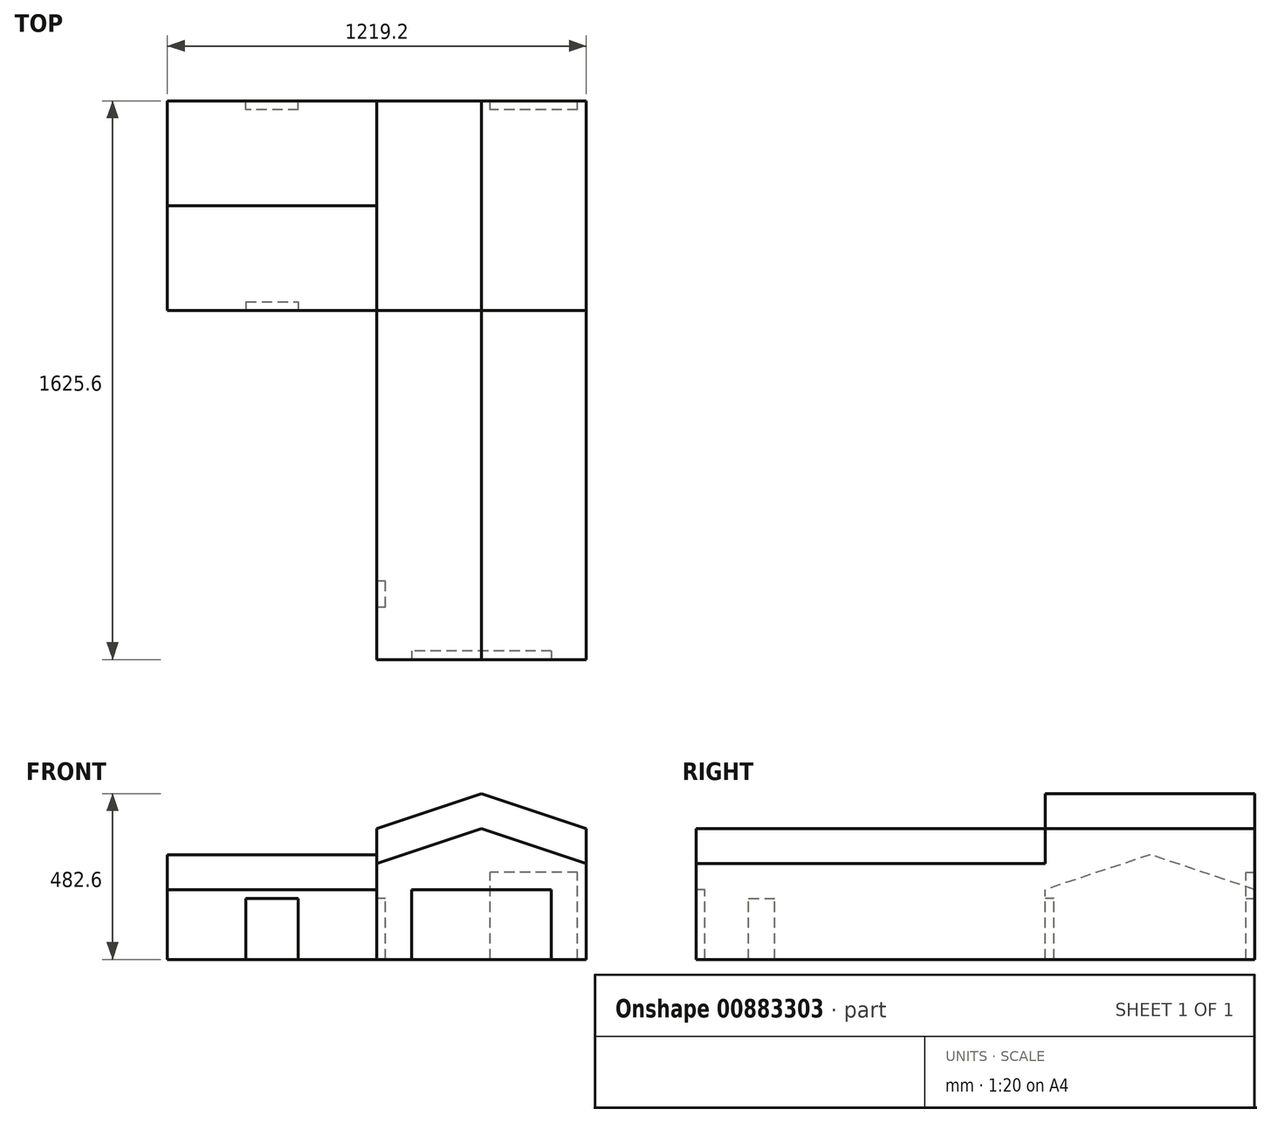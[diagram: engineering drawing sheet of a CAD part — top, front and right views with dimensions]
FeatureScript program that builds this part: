
annotation { "Feature Type Name" : "Feature", "Feature Type Description" : "" }
export const myFeature = defineFeature(function(context is Context, id is Id, definition is map)
    precondition{}
    {
        {
            var Q0;
            Q0=qCreatedBy(makeId("Front.planeOp"),FACE);
            var sketch = newSketch(context, id + "F0", { "sketchPlane" : qUnion([Q0])});
            skLineSegment(sketch, "E0", {"start": v(0, 0) * mm, "end": v(-304.8, 0) * mm});
            skLineSegment(sketch, "E1", {"start": v(-304.8, 0) * mm, "end": v(-304.8, 279.4) * mm});
            skLineSegment(sketch, "E2", {"start": v(-304.8, 279.4) * mm, "end": v(0, 381) * mm});
            skLineSegment(sketch, "E3", {"start": v(0, 381) * mm, "end": v(0, 0) * mm, "construction": true});
            skLineSegment(sketch, "E4.MirrorCS", {"start": v(304.8, 279.4) * mm, "end": v(0, 381) * mm});
            skLineSegment(sketch, "E5.MirrorCS", {"start": v(304.8, 0) * mm, "end": v(304.8, 279.4) * mm});
            skLineSegment(sketch, "E6.MirrorCS", {"start": v(0, 0) * mm, "end": v(304.8, 0) * mm});
            skSolve(sketch);
        }
        {
            var Q0;
            Q0=makeQuery(id+"F0.imprint","IMPRINT",FACE,{"disambiguationData":[TD([[makeQuery(id+"F0.imprint","IMPRINT",EDGE,{"derivedFrom":sQuery(id+"F0.wireOp",EDGE,"E0")}),-1.0]])]});
            extrude(context, id + "F1", {"entities" : qUnion([Q0]), "depth" : 1016 * mm, "offsetDistance" : 25.4 * mm});
        }
        {
            var Q0;
            Q0=makeQuery(id+"F1.opExtrude","CAP_FACE",FACE,{"disambiguationData":[OSD([sQuery(id+"F0.wireOp",EDGE,"E0"),sQuery(id+"F0.wireOp",EDGE,"E1"),sQuery(id+"F0.wireOp",EDGE,"E2"),sQuery(id+"F0.wireOp",EDGE,"E4.MirrorCS"),sQuery(id+"F0.wireOp",EDGE,"E5.MirrorCS"),sQuery(id+"F0.wireOp",EDGE,"E6.MirrorCS")])],"isStart":true});
            var sketch = newSketch(context, id + "F2", { "sketchPlane" : qUnion([Q0])});
            skLineSegment(sketch, "E7.0", {"start": v(-304.8, 0) * mm, "end": v(304.8, 0) * mm});
            skLineSegment(sketch, "E8", {"start": v(304.8, 381) * mm, "end": v(304.8, 0) * mm});
            skLineSegment(sketch, "E9", {"start": v(-304.8, 0) * mm, "end": v(-304.8, 381) * mm});
            skLineSegment(sketch, "E10", {"start": v(0, 0) * mm, "end": v(0, 482.6) * mm, "construction": true});
            skLineSegment(sketch, "E11", {"start": v(-304.8, 381) * mm, "end": v(0, 482.6) * mm});
            skLineSegment(sketch, "E12", {"start": v(0, 482.6) * mm, "end": v(304.8, 381) * mm});
            skSolve(sketch);
        }
        {
            var Q0;
            Q0 = qSketchRegion(id + "F2", true);
            extrude(context, id + "F3", {"entities" : qUnion([Q0]), "operationType" : NewBodyOperationType.ADD, "depth" : 609.6 * mm, "offsetDistance" : 25.4 * mm});
        }
        {
            var Q0;
            Q0=makeQuery(id+"F3.boolean.opBoolean","MERGE",FACE,{"derivedFrom":[makeQuery(id+"F1.opExtrude","SWEPT_FACE",FACE,{"disambiguationData":[OSD([sQuery(id+"F0.wireOp",EDGE,"E1")])]}),makeQuery(id+"F3.opExtrude","SWEPT_FACE",FACE,{"disambiguationData":[OSD([sQuery(id+"F2.wireOp",EDGE,"E8")])]})]});
            var sketch = newSketch(context, id + "F4", { "sketchPlane" : qUnion([Q0])});
            skLineSegment(sketch, "E13", {"start": v(-609.6, 0) * mm, "end": v(-609.6, 203.2) * mm});
            skLineSegment(sketch, "E14.0", {"start": v(-609.6, 381) * mm, "end": v(0, 381) * mm});
            skLineSegment(sketch, "E15", {"start": v(-304.8, 381) * mm, "end": v(-304.8, 0) * mm, "construction": true});
            skLineSegment(sketch, "E16.MirrorCS", {"start": v(0, 0) * mm, "end": v(0, 203.2) * mm});
            skLineSegment(sketch, "E17", {"start": v(-304.8, 0) * mm, "end": v(-304.8, 304.8) * mm});
            skLineSegment(sketch, "E18", {"start": v(-609.6, 203.2) * mm, "end": v(-304.8, 304.8) * mm});
            skLineSegment(sketch, "E19", {"start": v(-304.8, 304.8) * mm, "end": v(0, 203.2) * mm});
            skSolve(sketch);
        }
        {
            var Q0;
            {var subQ0=sQuery(id+"F4.wireOp",EDGE,"E13");Q0=makeQuery(id+"F4.imprint","IMPRINT",FACE,{"disambiguationData":[TD([[makeQuery(id+"F4.imprint","IMPRINT",EDGE,{"derivedFrom":subQ0}),-1.0]])]});}
            var Q1;
            {var subQ0=sQuery(id+"F4.wireOp",EDGE,"E16.MirrorCS");Q1=makeQuery(id+"F4.imprint","IMPRINT",FACE,{"disambiguationData":[TD([[makeQuery(id+"F4.imprint","IMPRINT",EDGE,{"derivedFrom":subQ0}),1.0]])]});}
            extrude(context, id + "F5", {"entities" : qUnion([Q0, Q1]), "operationType" : NewBodyOperationType.ADD, "depth" : 609.6 * mm, "offsetDistance" : 25.4 * mm});
        }
        {
            var Q0;
            Q0=makeQuery(id+"F5.opExtrude","SWEPT_FACE",FACE,{"disambiguationData":[OSD([sQuery(id+"F4.wireOp",EDGE,"E16.MirrorCS")])]});
            var sketch = newSketch(context, id + "F6", { "sketchPlane" : qUnion([Q0])});
            skLineSegment(sketch, "E20", {"start": v(-609.6, 0) * mm, "end": v(-609.6, 177.8) * mm, "construction": true});
            skLineSegment(sketch, "E21.0", {"start": v(-685.8, 0) * mm, "end": v(-685.8, 177.8) * mm});
            skLineSegment(sketch, "E22.0", {"start": v(-533.4, 0) * mm, "end": v(-533.4, 177.8) * mm});
            skLineSegment(sketch, "E23.0", {"start": v(-685.8, 177.8) * mm, "end": v(-533.4, 177.8) * mm});
            skPoint(sketch, "E24.orphan", {"position": v(-609.6, 203.2) * mm});
            skSolve(sketch);
        }
        {
            var Q0;
            {var subQ0=sQuery(id+"F6.wireOp",EDGE,"E21.0");Q0=makeQuery(id+"F6.imprint","IMPRINT",FACE,{"disambiguationData":[TD([[makeQuery(id+"F6.imprint","IMPRINT",EDGE,{"derivedFrom":subQ0}),-1.0]])]});}
            extrude(context, id + "F7", {"entities" : qUnion([Q0]), "operationType" : NewBodyOperationType.REMOVE, "oppositeDirection" : true, "depth" : 25.4 * mm, "offsetDistance" : 25.4 * mm});
        }
        {
            var Q0;
            Q0=makeQuery(id+"F1.opExtrude","CAP_FACE",FACE,{"disambiguationData":[OSD([sQuery(id+"F0.wireOp",EDGE,"E0"),sQuery(id+"F0.wireOp",EDGE,"E1"),sQuery(id+"F0.wireOp",EDGE,"E2"),sQuery(id+"F0.wireOp",EDGE,"E4.MirrorCS"),sQuery(id+"F0.wireOp",EDGE,"E5.MirrorCS"),sQuery(id+"F0.wireOp",EDGE,"E6.MirrorCS")])],"isStart":false});
            var sketch = newSketch(context, id + "F8", { "sketchPlane" : qUnion([Q0])});
            skLineSegment(sketch, "E25", {"start": v(0, 0) * mm, "end": v(0, 203.2) * mm, "construction": true});
            skLineSegment(sketch, "E26.0", {"start": v(-203.2, 0) * mm, "end": v(-203.2, 203.2) * mm});
            skLineSegment(sketch, "E27.0", {"start": v(203.2, 0) * mm, "end": v(203.2, 203.2) * mm});
            skLineSegment(sketch, "E28.0", {"start": v(203.2, 203.2) * mm, "end": v(-203.2, 203.2) * mm});
            skSolve(sketch);
        }
        {
            var Q0;
            {var subQ0=sQuery(id+"F8.wireOp",EDGE,"E26.0");Q0=makeQuery(id+"F8.imprint","IMPRINT",FACE,{"disambiguationData":[TD([[makeQuery(id+"F8.imprint","IMPRINT",EDGE,{"derivedFrom":subQ0}),-1.0]])]});}
            extrude(context, id + "F9", {"entities" : qUnion([Q0]), "operationType" : NewBodyOperationType.REMOVE, "oppositeDirection" : true, "depth" : 25.4 * mm, "offsetDistance" : 25.4 * mm});
        }
        {
            var Q0;
            Q0=makeQuery(id+"F5.boolean.opBoolean","MERGE",FACE,{"derivedFrom":[makeQuery(id+"F3.opExtrude","CAP_FACE",FACE,{"disambiguationData":[OSD([sQuery(id+"F2.wireOp",EDGE,"E7.0"),sQuery(id+"F2.wireOp",EDGE,"E8"),sQuery(id+"F2.wireOp",EDGE,"E9"),sQuery(id+"F2.wireOp",EDGE,"E11"),sQuery(id+"F2.wireOp",EDGE,"E12")])],"isStart":false}),makeQuery(id+"F5.opExtrude","SWEPT_FACE",FACE,{"disambiguationData":[OSD([sQuery(id+"F4.wireOp",EDGE,"E13")])]})]});
            var sketch = newSketch(context, id + "F10", { "sketchPlane" : qUnion([Q0])});
            skLineSegment(sketch, "E29.0", {"start": v(-279.4, 0) * mm, "end": v(-279.4, 254) * mm});
            skLineSegment(sketch, "E30.0", {"start": v(-25.4, 0) * mm, "end": v(-25.4, 254) * mm});
            skLineSegment(sketch, "E31.0", {"start": v(-279.4, 254) * mm, "end": v(-25.4, 254) * mm});
            skLineSegment(sketch, "E32.0", {"start": v(685.8, 0) * mm, "end": v(685.8, 177.8) * mm});
            skLineSegment(sketch, "E33.0", {"start": v(533.4, 0) * mm, "end": v(533.4, 177.8) * mm});
            skLineSegment(sketch, "E34.0", {"start": v(-304.8, 203.2) * mm, "end": v(-25.4, 203.2) * mm});
            skLineSegment(sketch, "E35.0", {"start": v(685.8, 177.8) * mm, "end": v(533.4, 177.8) * mm});
            skSolve(sketch);
        }
        {
            var Q0;
            {var subQ0=sQuery(id+"F10.wireOp",EDGE,"E29.0");Q0=makeQuery(id+"F10.imprint","IMPRINT",FACE,{"disambiguationData":[TD([[makeQuery(id+"F10.imprint","IMPRINT",EDGE,{"derivedFrom":subQ0}),-1.0]])]});}
            var Q1;
            {var subQ0=sQuery(id+"F10.wireOp",EDGE,"E32.0");Q1=makeQuery(id+"F10.imprint","IMPRINT",FACE,{"disambiguationData":[TD([[makeQuery(id+"F10.imprint","IMPRINT",EDGE,{"derivedFrom":subQ0}),1.0]])]});}
            extrude(context, id + "F11", {"entities" : qUnion([Q0, Q1]), "operationType" : NewBodyOperationType.REMOVE, "oppositeDirection" : true, "depth" : 25.4 * mm, "offsetDistance" : 25.4 * mm});
        }
        {
            var Q0;
            Q0=makeQuery(id+"F3.boolean.opBoolean","MERGE",FACE,{"derivedFrom":[makeQuery(id+"F1.opExtrude","SWEPT_FACE",FACE,{"disambiguationData":[OSD([sQuery(id+"F0.wireOp",EDGE,"E1")])]}),makeQuery(id+"F3.opExtrude","SWEPT_FACE",FACE,{"disambiguationData":[OSD([sQuery(id+"F2.wireOp",EDGE,"E8")])]})]});
            var sketch = newSketch(context, id + "F12", { "sketchPlane" : qUnion([Q0])});
            skLineSegment(sketch, "E36.0", {"start": v(863.6, 0) * mm, "end": v(863.6, 177.8) * mm});
            skLineSegment(sketch, "E37.0", {"start": v(787.4, 0) * mm, "end": v(787.4, 177.8) * mm});
            skLineSegment(sketch, "E38.0", {"start": v(863.6, 177.8) * mm, "end": v(787.4, 177.8) * mm});
            skSolve(sketch);
        }
        {
            var Q0;
            {var subQ0=sQuery(id+"F12.wireOp",EDGE,"E36.0");Q0=makeQuery(id+"F12.imprint","IMPRINT",FACE,{"disambiguationData":[TD([[makeQuery(id+"F12.imprint","IMPRINT",EDGE,{"derivedFrom":subQ0}),1.0]])]});}
            extrude(context, id + "F13", {"entities" : qUnion([Q0]), "operationType" : NewBodyOperationType.REMOVE, "oppositeDirection" : true, "depth" : 25.4 * mm, "offsetDistance" : 25.4 * mm});
        }
    });
